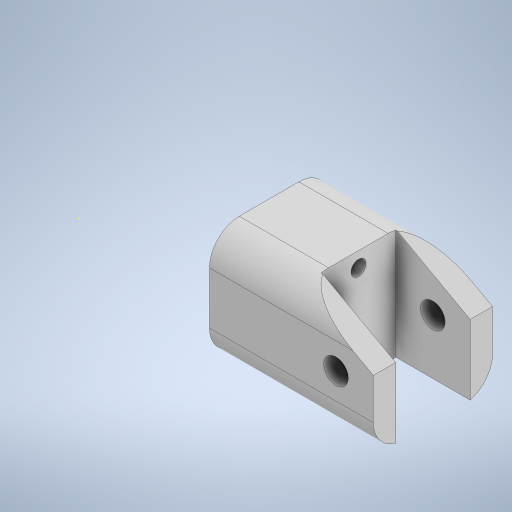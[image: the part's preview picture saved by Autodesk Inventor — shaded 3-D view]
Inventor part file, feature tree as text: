
AUTODESK INVENTOR PART (.ipt)
format: ipt  version: 2024 (Build 280153020, 153B)  size: 430,080 bytes
history: native  units: mm
features: sketch x21, extrude x18, chamfer x3, plane x1, split x1, move_body x1, delete_face x1, fillet x1
ambient origin geometry x8: Origin, YZ Plane, XZ Plane, XY Plane, X Axis, Y Axis, Z Axis, Center Point
bodies: Solid1 (feature_tree), Solid2 (feature_tree), Solid3 (feature_tree)
feature tree (47):
  extrude  "Extrusion1"  Depth=16.0mm
  sketch  "Sketch2"  dims[d2=15.0mm d3=0.0mm d4=10.0mm]
  extrude  "Extrusion2"  Depth=10.0mm
  chamfer  "Chamfer1"  Distance=21.25mm
  extrude  "Extrusion3"  Depth=10.0mm TaperAngle=0.0deg
  extrude  "Extrusion4"  Depth=11.5mm TaperAngle=0.0deg
  extrude  "Extrusion5"  Depth=1.0mm TaperAngle=0.0deg
  chamfer  "Chamfer2"  Distance=11.5mm Angle=45.0deg
  sketch  "Sketch6"  dims[d14=7.0mm d15=11.5mm d16=0.0mm]
  extrude  "Extrusion6"  Depth=15.0mm
  extrude  "Extrusion7"  Depth=5.5mm TaperAngle=0.0deg
  chamfer  "Chamfer3"  Distance=11.5mm Angle=45.0deg
  sketch  "Sketch9"  dims[d26=3.3mm d27=45.25mm d28=0.0mm d29=11.5mm d30=5.5mm d31=45.0deg]
  extrude  "Extrusion8"  Depth=65.75mm TaperAngle=0.0deg
  extrude  "Extrusion9"  Depth=0.5mm TaperAngle=0.0deg
  extrude  "Extrusion10"  Depth=13.0mm TaperAngle=0.0deg
  sketch  "Sketch13"  dims[d43=24.0mm d44=21.0mm d45=0.0mm]
  extrude  "Extrusion11"  Depth=21.0mm TaperAngle=0.0deg
  extrude  "Extrusion12"  TaperAngle=0.0deg  [1 undecoded]
  extrude  "Extrusion13"  Depth=4.0mm
  plane  "Work Plane1"
  split  "Split1"
  move_body  "Move Body1"
  extrude  "Extrusion14"  Depth=1.0mm
  delete_face  "Delete Face1"
  fillet  "Fillet1"  Radius=1.5mm
  extrude  "Extrusion17"  Depth=1.0mm
  extrude  "Extrusion18"  Depth=5.5mm TaperAngle=0.0deg
  extrude  "Extrusion19"  Depth=0.872665mm
  extrude  "Extrusion20"  [1 undecoded]
  sketch  "Sketch1"  dims[d0=36.0mm d1=16.0mm]
  sketch  "Sketch3"  dims[d5=10.0mm]
  sketch  "Sketch4"  dims[d6=3.3mm d7=21.25mm d8=0.0mm]
  sketch  "Sketch5"  dims[d9=10.0mm d10=5.5mm d11=45.0deg d12=10.0mm d13=0.0mm]
  sketch  "Sketch7"  dims[d17=3.3mm d18=1.0mm d19=0.0mm d20=6.0mm d21=11.5mm d22=45.0deg]
  sketch  "Sketch8"  dims[d23=15.0mm d24=0.0mm d25=9.0mm]
  sketch  "Sketch10"  dims[d32=2.0mm d33=65.75mm d34=0.0mm]
  sketch  "Sketch11"  dims[d35=0.5mm d36=0.0mm d37=9.0mm d38=0.0mm]
  sketch  "Sketch12"  dims[d39=0.5mm d40=0.0mm d41=13.0mm d42=0.0mm]
  sketch  "Sketch14"  dims[d46=12.25mm d47=-12.0mm d48=0.0mm d49=0.0mm]
  sketch  "Sketch15"  dims[d50=10.0mm d51=0.0mm d52=4.0mm]
  sketch  "Sketch16"  dims[d61=1.0mm d62=1.0mm d63=1.5mm d64=0.0mm]
  sketch  "Sketch17"  dims[d65=1.0mm d66=1.0mm]
  sketch  "Sketch20"  dims[d67=5.5mm d68=0.0mm d69=1.2mm d70=0.0mm]
  sketch  "Sketch21"  dims[d71=2.2mm d72=0.0mm d53=0.872665mm]
  sketch  "Sketch22"
  sketch  "Sketch23"
note: 2 required parameter values undecoded (feature->parameter linkage not recoverable at this tier; creation-order binding heuristic only, values carry confidence <= 0.55)
